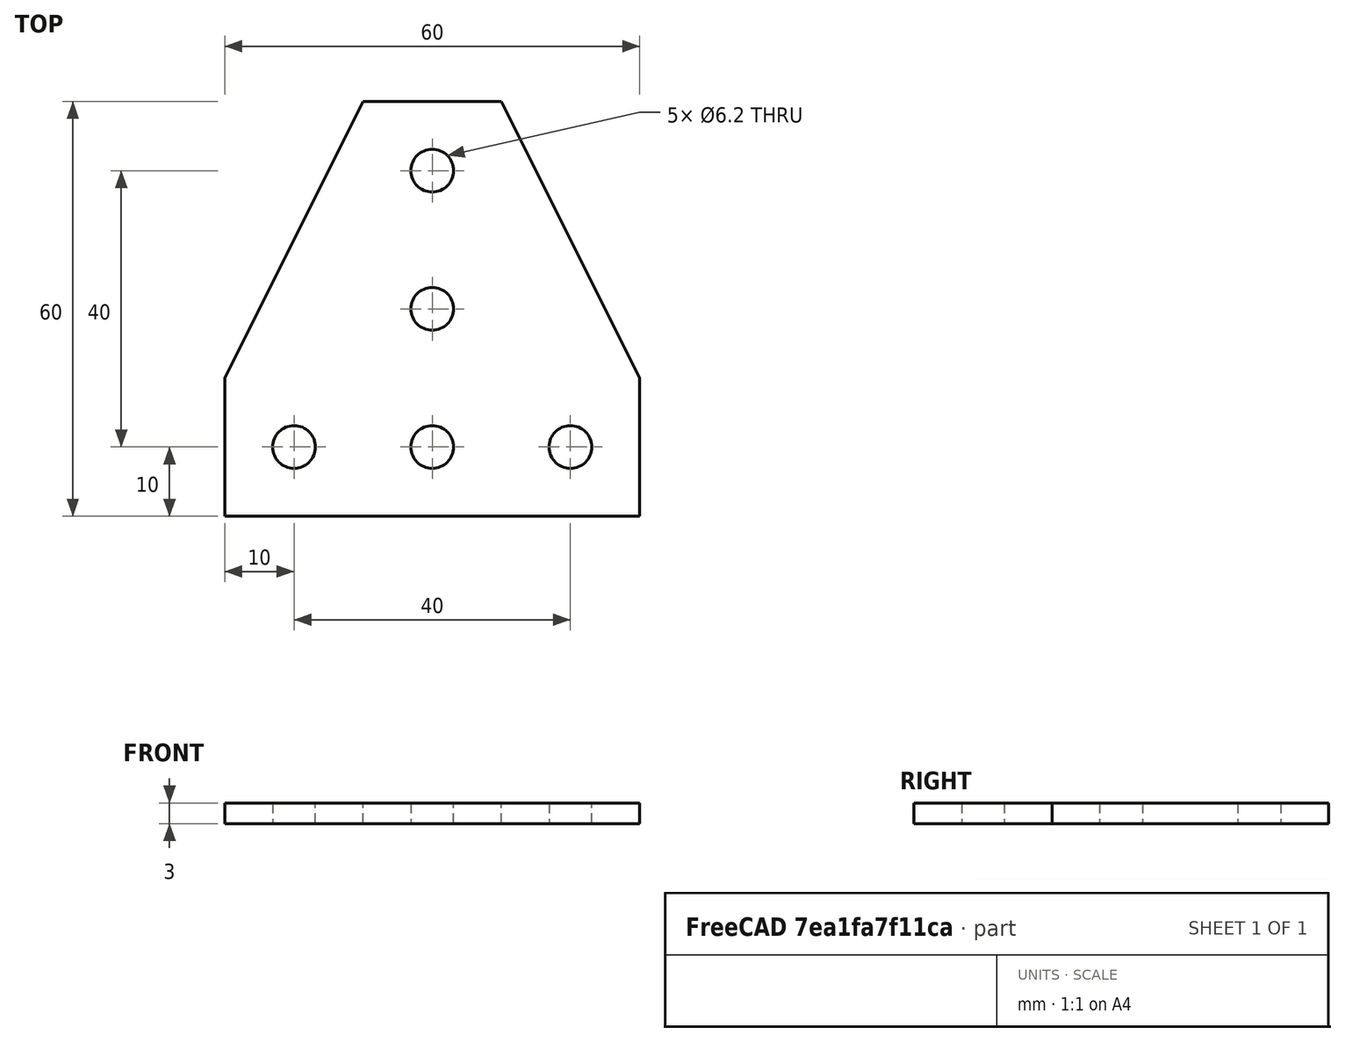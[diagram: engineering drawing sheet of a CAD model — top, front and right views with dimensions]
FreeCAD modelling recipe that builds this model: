
FCSTD DOCUMENT  (FreeCAD 0.17R9796 (Git))
Label: tcon
License: All rights reserved
LicenseURL: http://en.wikipedia.org/wiki/All_rights_reserved
objects: Sketcher::SketchObject×1, PartDesign::Pad×1, PartDesign::Body×1
note: 4 computed .brp shape members not serialized (recipe doc carries the construction recipe); baked Part::Feature solids carry a one-line shape summary decoded from their .brp

FEATURE [Sketcher::SketchObject] Sketch
  MapMode = 5
  Support = -> [XY_Plane]
  sketch-geometry (11):
    g0: LineSegment StartX=0 StartY=0 StartZ=0 EndX=60 EndY=0 EndZ=0
    g1: LineSegment StartX=60 StartY=0 StartZ=0 EndX=60 EndY=20 EndZ=0
    g2: LineSegment StartX=60 StartY=20 StartZ=0 EndX=40 EndY=60 EndZ=0
    g3: LineSegment StartX=40 StartY=60 StartZ=0 EndX=20 EndY=60 EndZ=0
    g4: LineSegment StartX=20 StartY=60 StartZ=0 EndX=0 EndY=20 EndZ=0
    g5: LineSegment StartX=0 StartY=20 StartZ=0 EndX=0 EndY=0 EndZ=0
    g6: Circle CenterX=10 CenterY=10 CenterZ=0 NormalX=0 NormalY=0 NormalZ=1 Radius=3.1
    g7: Circle CenterX=30 CenterY=10 CenterZ=0 NormalX=0 NormalY=0 NormalZ=1 Radius=3.1
    g8: Circle CenterX=50 CenterY=10 CenterZ=0 NormalX=0 NormalY=0 NormalZ=1 Radius=3.1
    g9: Circle CenterX=30 CenterY=30 CenterZ=0 NormalX=0 NormalY=0 NormalZ=1 Radius=3.1
    g10: Circle CenterX=30 CenterY=50 CenterZ=0 NormalX=0 NormalY=0 NormalZ=1 Radius=3.1
  constraints (32):
    c: Coincident(g0,g1)
    c: Coincident(g1,g2)
    c: Coincident(g2,g3)
    c: Coincident(g3,g4)
    c: Coincident(g4,g5)
    c: Coincident(g5,g0)
    c: Horizontal(g0)
    c: Vertical(g5)
    c: Vertical(g1)
    c: Horizontal(g3)
    c: Coincident(g0,g-1)
    c: DistanceX(g0,g0) = 60
    c: DistanceY(g5,g5) = 20
    c: DistanceY(g0,g1) = 20
    c: DistanceY(g-1,g3) = 60
    c: DistanceX(g-1,g3) = 20
    c: DistanceX(g3,g2) = 20
    c: Radius(g6) = 3.1
    c: DistanceY(g-1,g6) = 10
    c: DistanceX(g-1,g6) = 10
    c: DistanceY(g6,g7) = 0
    c: DistanceY(g7,g8) = 0
    c: DistanceX(g6,g7) = 20
    c: DistanceX(g7,g8) = 20
    c: DistanceX(g9,g7) = 0
    c: DistanceX(g10,g9) = 0
    c: DistanceY(g9,g10) = 20
    c: DistanceY(g7,g9) = 20
    c: Radius(g10) = 3.1
    c: Radius(g9) = 3.1
    c: Radius(g7) = 3.1
    c: Radius(g8) = 3.1
FEATURE [PartDesign::Pad] Pad
  Length = 3
  Length2 = 100
  Profile = -> Sketch
  Type = 0
FEATURE [PartDesign::Body] Body
  Group = -> [Sketch,Pad]
  Origin = -> BodyOrigin
  Tip = -> Pad
